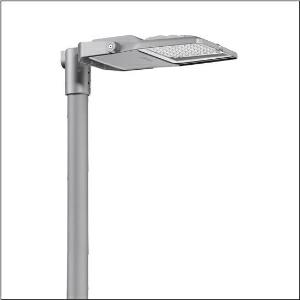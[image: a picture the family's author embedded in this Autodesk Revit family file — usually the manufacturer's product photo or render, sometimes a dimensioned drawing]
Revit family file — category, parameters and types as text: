
# Revit family: floodlight_fl_21_mini___pl52_5xa7776c2d3a_1d2c
name_source: partatom
category: Lighting Fixtures
units: mm (PartAtom-declared; Revit-internal decimal feet)

## family parameters
Cut with Voids When Loaded = No
Host = Face
Light Source = No
Part Type = Normal
Room Calculation Point = No
Round Connector Dimension = Use Diameter
Shared = No

## types (1)
- --- (1 x LED, 12190 lm, 89 W, 3000K)
    Apparent Load = 89 VA
    CIE Flux Codes = 26 60 98 100 100
    Color Rendering = 70
    Color Temperature = 3000K
    Default Elevation = 1800 mm
    Description = Floodlight FL 21 mini, floodlight, primary light control with lens, of PMMA, primary optical cover: protective disc, of toughened safety glass, transparent, light distribution: PL52, light emission: direct distribution, installation type: surface-mounted, LED, High Power LED, rated luminous flux: 12.190lm, luminous efficacy: 137lm/W, light colour: 730, colour temperature: 3000K, control: flexible luminous flux parameterisation, time-dependent luminous flux control, constant luminous flux control, overheat protection, presetting dimming logarithmic, with terminal, 6-pole, mains connection: 220..240V, AC, 50/60Hz, start of lifetime: 89W, end of service life: 94W, reduction: 43W, luminaire housing, of diecast aluminium, powder-coated, Siteco® metallic grey (DB 702S), corrosivity category C5 mid according to DIN EN ISO 12944, sealing non-destructively replaceable, please order mast flange separately, mast bracket, of steel, galvanised, powder-coated, Siteco® metallic grey (DB 702S), Smart Interface below and above, protection rating (complete): IP66, insulation class (complete): insulation class II (safety insulation), certification: CE, ENEC, VDE, protection symbol: D, impact resistance: IK08, permissible operating ambient temperature: -40..+40°C, permissible operating ambient temperature for outdoor applications: -40..+50°C, standard: DIN EN 12944, LABS conformity tested according to VDMA 24364:2018-05, packaging unit: 1 piece

Light Distribution: PL52
    Height = 70 mm
    Lamp = 1 x LED
    Lamp Light Flux = 12190 lm
    Lamp Power = 89 W
    Lamp count = 1
    Length = 485 mm
    Luminous efficacy = 137 lm/W
    Manufacturer = Siteco
    ModVariant = No
    Model = 5XA7776C2D3A
    Number of Poles = 1
    OnlyDefault = Yes
    Power Factor = 1
    Product Name = Floodlight FL 21 mini | PL52
    Product group = floodlight | pylon annexe
    ProductGroupID = 6200
    Protection Class = Protection class II
    Protection Degree = IP 66
    RLX_Detail_Level = 1
    RLX_Emergency_Light_Flux = 0 lm
    RLX_Emergency_Type = 0
    RLX_Emergency_Type_DB = No
    RlxData = <blob elided: 101001 chars, md5=0497953f>
    Socket = socket
    Standby Power = 0 W
    System Light Flux = 12190 lm
    System Power = 89 W
    Type Comments = factory setting: luminous flux: 100 % | dim-lin: 254 | 456 mA
    Type Image = l_1007125.jpg
    URL = http://relux.com
    VarID = @adj_095557
    Voltage = 0 V
    Weight = 0.00 kg
    Width = 337 mm

## geometry (parser evidence)
native form markers: Blend x4, Sweep x15
no freeform markers — native parametric forms only
